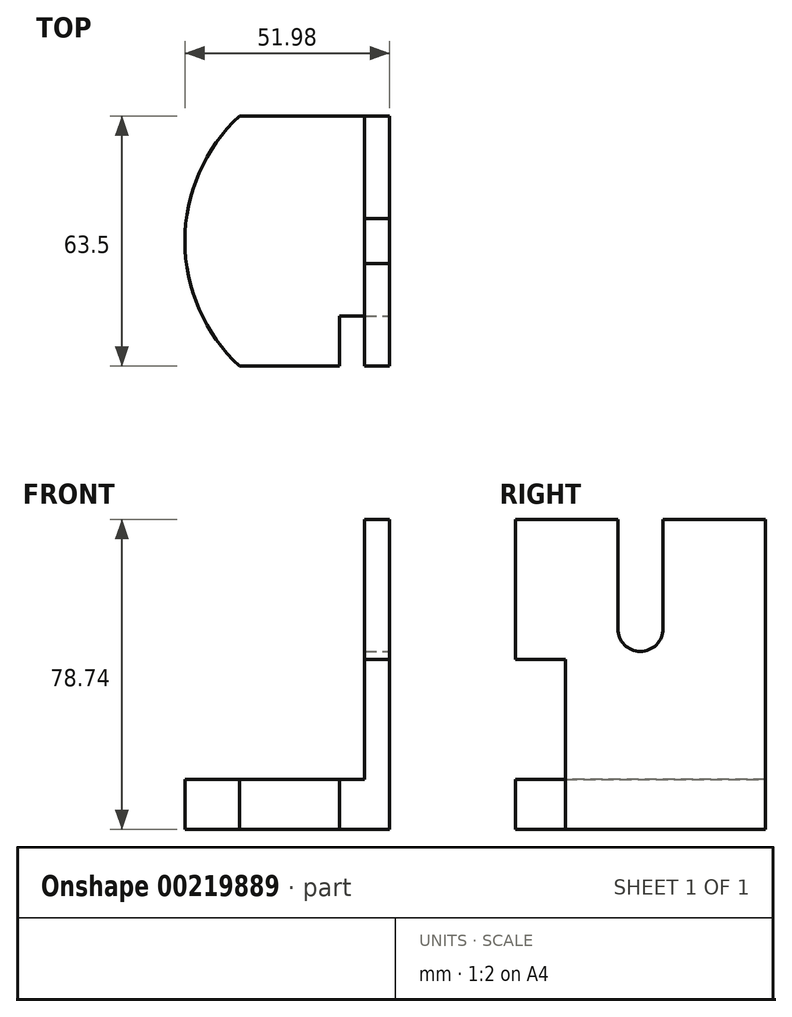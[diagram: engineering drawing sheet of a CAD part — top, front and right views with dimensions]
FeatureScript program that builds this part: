
annotation { "Feature Type Name" : "Feature", "Feature Type Description" : "" }
export const myFeature = defineFeature(function(context is Context, id is Id, definition is map)
    precondition{}
    {
        {
            var Q0;
            Q0=qCreatedBy(makeId("Top.planeOp"),FACE);
            var sketch = newSketch(context, id + "F0", { "sketchPlane" : qUnion([Q0])});
            skLineSegment(sketch, "E0", {"start": v(0, 0) * mm, "end": v(0, 50.8) * mm});
            skLineSegment(sketch, "E1", {"start": v(0, 50.8) * mm, "end": v(-38.1, 50.8) * mm});
            skLineSegment(sketch, "E2", {"start": v(0, 0) * mm, "end": v(-12.7, 0) * mm});
            skLineSegment(sketch, "E3", {"start": v(-12.7, 0) * mm, "end": v(-12.7, -12.7) * mm});
            skLineSegment(sketch, "E4", {"start": v(-12.7, -12.7) * mm, "end": v(-38.1, -12.7) * mm});
            skArc(sketch, "E5", {"start": v(-38.1, 50.8) * mm, "mid": v(-51.98, 19.05) * mm, "end": v(-38.1, -12.7) * mm});
            skSolve(sketch);
        }
        {
            var Q0;
            Q0 = qSketchRegion(id + "F0", true);
            extrude(context, id + "F1", {"entities" : qUnion([Q0]), "depth" : 12.7 * mm});
        }
        {
            var Q0;
            Q0=makeQuery(id+"F1.opExtrude","SWEPT_FACE",FACE,{"disambiguationData":[OSD([sQuery(id+"F0.wireOp",EDGE,"E0")])]});
            var sketch = newSketch(context, id + "F2", { "sketchPlane" : qUnion([Q0])});
            skLineSegment(sketch, "E6", {"start": v(0, 0) * mm, "end": v(0, 43.18) * mm});
            skLineSegment(sketch, "E7", {"start": v(0, 43.18) * mm, "end": v(-12.7, 43.18) * mm});
            skLineSegment(sketch, "E8", {"start": v(-12.7, 43.18) * mm, "end": v(-12.7, 78.74) * mm});
            skLineSegment(sketch, "E9", {"start": v(-12.7, 78.74) * mm, "end": v(50.8, 78.74) * mm});
            skPoint(sketch, "E9.endSnap0", {"position": v(50.8, 6.35) * mm});
            skLineSegment(sketch, "E10", {"start": v(50.8, 78.74) * mm, "end": v(50.8, 0) * mm});
            skLineSegment(sketch, "E11", {"start": v(50.8, 0) * mm, "end": v(0, 0) * mm});
            skArc(sketch, "E12", {"start": v(13.3, 50.98) * mm, "mid": v(19.05, 45.23) * mm, "end": v(24.8, 50.98) * mm});
            skPoint(sketch, "E12.centerSnap0", {"position": v(19.05, 78.74) * mm});
            skLineSegment(sketch, "E13", {"start": v(13.3, 50.98) * mm, "end": v(13.3, 78.74) * mm});
            skLineSegment(sketch, "E14", {"start": v(24.8, 50.98) * mm, "end": v(24.8, 78.74) * mm});
            skSolve(sketch);
        }
        {
            var Q0;
            {var subQ3=sQuery(id+"F2.wireOp",EDGE,"E7");Q0=makeQuery(id+"F2.imprint","IMPRINT",FACE,{"disambiguationData":[TD([[makeQuery(id+"F2.imprint","IMPRINT",EDGE,{"derivedFrom":subQ3}),-1.0]])]});}
            extrude(context, id + "F3", {"entities" : qUnion([Q0]), "operationType" : NewBodyOperationType.ADD, "oppositeDirection" : true, "depth" : 6.35 * mm});
        }
    });
